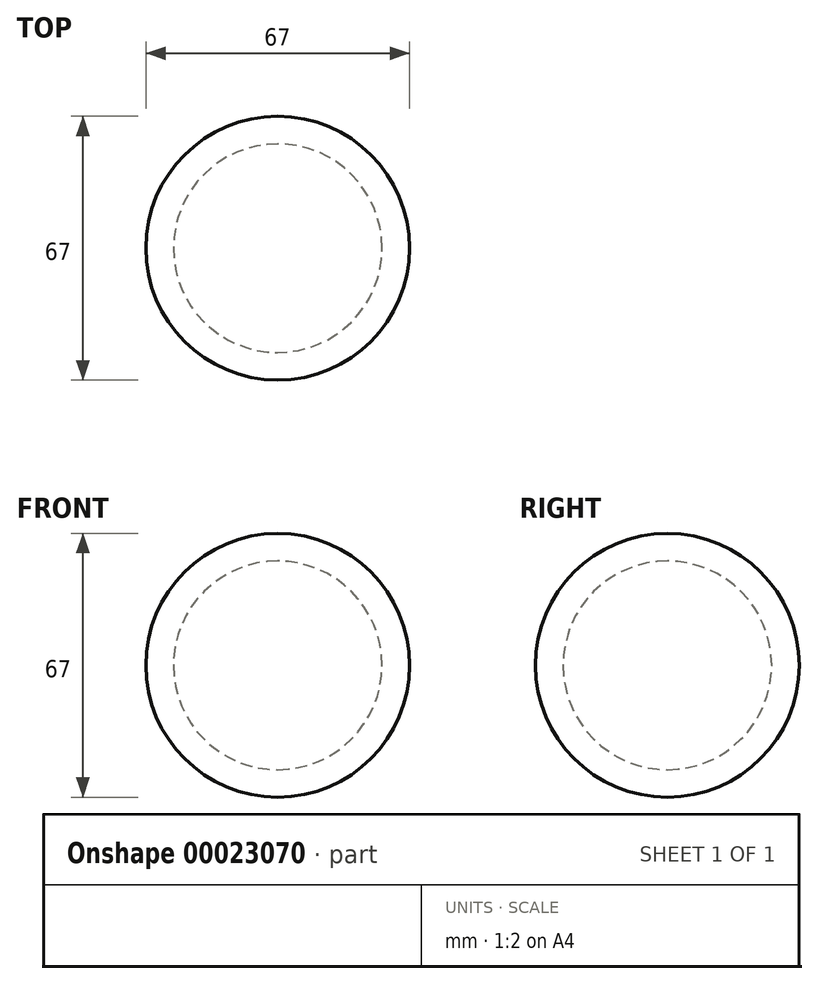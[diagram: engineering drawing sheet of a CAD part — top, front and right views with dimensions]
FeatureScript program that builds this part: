
annotation { "Feature Type Name" : "Feature", "Feature Type Description" : "" }
export const myFeature = defineFeature(function(context is Context, id is Id, definition is map)
    precondition{}
    {
        {
            var Q0;
            Q0=qCreatedBy(makeId("Front.planeOp"),FACE);
            var sketch = newSketch(context, id + "F0", { "sketchPlane" : qUnion([Q0])});
            skArc(sketch, "E0", {"start": v(0, -33.5) * mm, "mid": v(33.5, 0) * mm, "end": v(0, 33.5) * mm});
            skArc(sketch, "E1", {"start": v(0, -26.5) * mm, "mid": v(26.5, 0) * mm, "end": v(0, 26.5) * mm});
            skLineSegment(sketch, "E2", {"start": v(0, 33.5) * mm, "end": v(0, 26.5) * mm});
            skLineSegment(sketch, "E3.trimOffspring", {"start": v(0, -26.5) * mm, "end": v(0, -33.5) * mm});
            skSolve(sketch);
        }
        {
            var Q0;
            Q0 = qSketchRegion(id + "F0", true);
            var Q1;
            Q1=sQuery(id+"F0.wireOp",EDGE,"E2");
            revolve(context, id + "F1", {"entities" : qUnion([Q0]), "axis" : qUnion([Q1]), "revolveType" : RevolveType.FULL});
        }
    });
